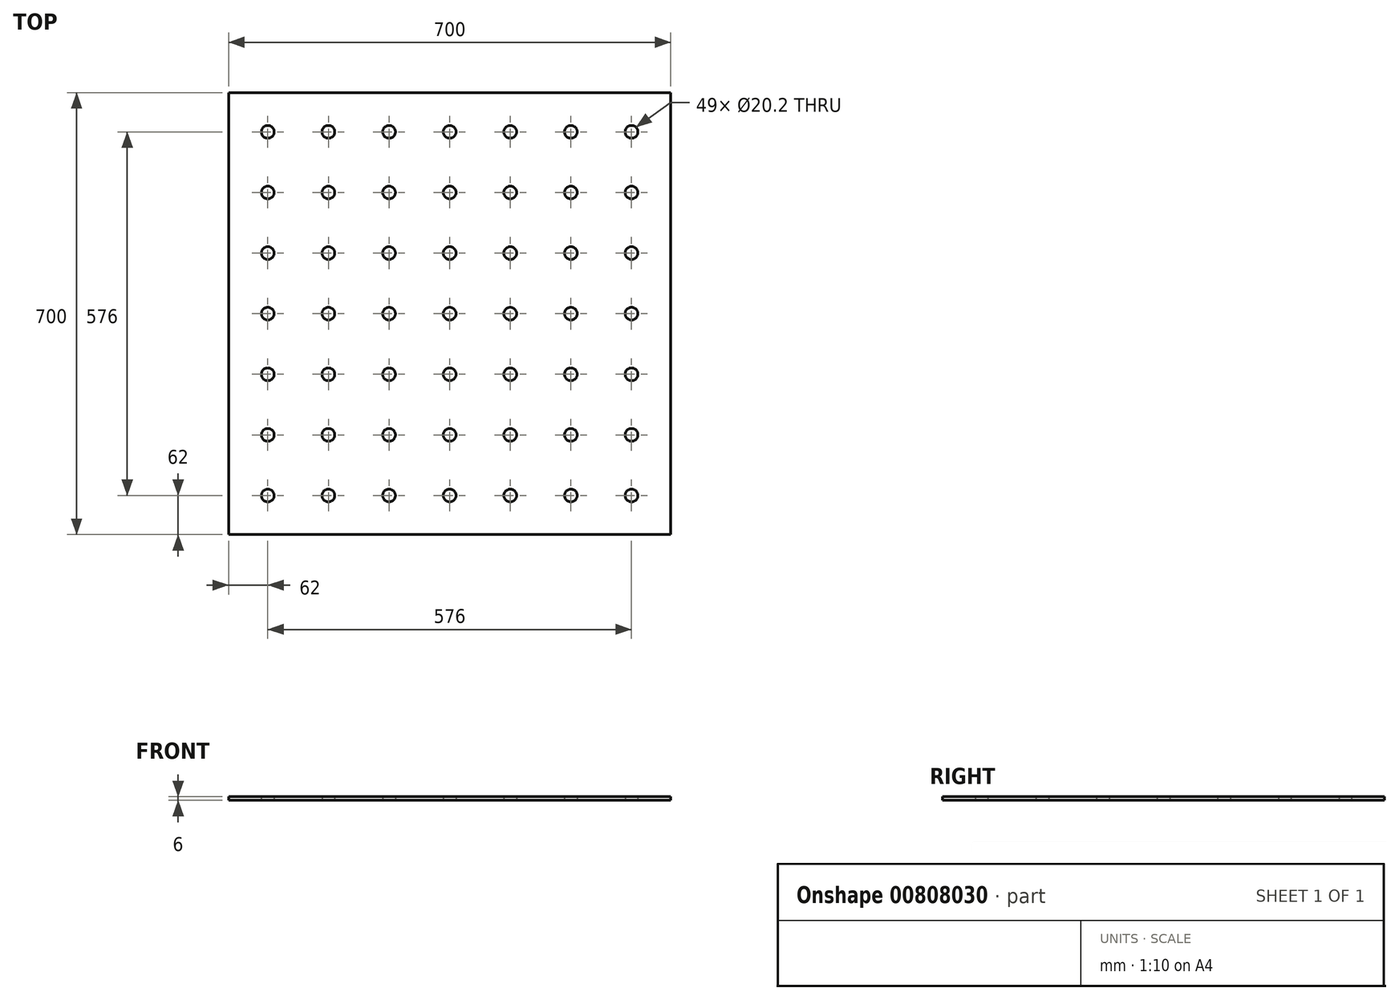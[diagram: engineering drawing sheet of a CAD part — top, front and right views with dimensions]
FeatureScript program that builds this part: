
annotation { "Feature Type Name" : "Feature", "Feature Type Description" : "" }
export const myFeature = defineFeature(function(context is Context, id is Id, definition is map)
    precondition{}
    {
        {
            var Q0;
            Q0=qCreatedBy(makeId("Top.planeOp"),FACE);
            var sketch = newSketch(context, id + "F0", { "sketchPlane" : qUnion([Q0])});
            skLineSegment(sketch, "E0.bottom", {"start": v(-350, 350) * mm, "end": v(350, 350) * mm});
            skLineSegment(sketch, "E0.top", {"start": v(-350, -350) * mm, "end": v(350, -350) * mm});
            skLineSegment(sketch, "E0.left", {"start": v(-350, 350) * mm, "end": v(-350, -350) * mm});
            skLineSegment(sketch, "E0.right", {"start": v(350, 350) * mm, "end": v(350, -350) * mm});
            skPoint(sketch, "E0.middle", {"position": v(0, 0) * mm});
            skLineSegment(sketch, "E1", {"start": v(0, 350) * mm, "end": v(0, -350) * mm, "construction": true});
            skCircle(sketch, "E2", {"center": v(0, 0) * mm, "radius": 10.1 * mm});
            skCircle(sketch, "E3.1.0.0", {"center": v(96, 0) * mm, "radius": 10.1 * mm});
            skCircle(sketch, "E3.2.0.0", {"center": v(192, 0) * mm, "radius": 10.1 * mm});
            skLineSegment(sketch, "E3.direction1", {"start": v(0, 0) * mm, "end": v(96, 0) * mm, "construction": true});
            skCircle(sketch, "E4.0.3.0", {"center": v(288, 0) * mm, "radius": 10.1 * mm});
            skCircle(sketch, "E5.MirrorC", {"center": v(-96, 0) * mm, "radius": 10.1 * mm});
            skCircle(sketch, "E6.MirrorC", {"center": v(-192, 0) * mm, "radius": 10.1 * mm});
            skCircle(sketch, "E7.MirrorC", {"center": v(-288, 0) * mm, "radius": 10.1 * mm});
            skCircle(sketch, "E8", {"center": v(0, 96) * mm, "radius": 10.1 * mm});
            skCircle(sketch, "E9", {"center": v(0, 192) * mm, "radius": 10.1 * mm});
            skCircle(sketch, "E10", {"center": v(0, 288) * mm, "radius": 10.1 * mm});
            skCircle(sketch, "E11.1.0.0", {"center": v(96, 96) * mm, "radius": 10.1 * mm});
            skCircle(sketch, "E11.2.0.0", {"center": v(192, 96) * mm, "radius": 10.1 * mm});
            skCircle(sketch, "E11.3.0.0", {"center": v(288, 96) * mm, "radius": 10.1 * mm});
            skLineSegment(sketch, "E11.direction1", {"start": v(0, 96) * mm, "end": v(96, 96) * mm, "construction": true});
            skCircle(sketch, "E12.1.0.0", {"center": v(96, 192) * mm, "radius": 10.1 * mm});
            skCircle(sketch, "E12.2.0.0", {"center": v(192, 192) * mm, "radius": 10.1 * mm});
            skCircle(sketch, "E12.3.0.0", {"center": v(288, 192) * mm, "radius": 10.1 * mm});
            skLineSegment(sketch, "E12.direction1", {"start": v(0, 192) * mm, "end": v(96, 192) * mm, "construction": true});
            skCircle(sketch, "E13.1.0.0", {"center": v(96, 288) * mm, "radius": 10.1 * mm});
            skCircle(sketch, "E13.2.0.0", {"center": v(192, 288) * mm, "radius": 10.1 * mm});
            skCircle(sketch, "E13.3.0.0", {"center": v(288, 288) * mm, "radius": 10.1 * mm});
            skLineSegment(sketch, "E13.direction1", {"start": v(0, 288) * mm, "end": v(96, 288) * mm, "construction": true});
            skCircle(sketch, "E14.MirrorC", {"center": v(-96, 288) * mm, "radius": 10.1 * mm});
            skCircle(sketch, "E15.MirrorC", {"center": v(-192, 288) * mm, "radius": 10.1 * mm});
            skCircle(sketch, "E16.MirrorC", {"center": v(-288, 288) * mm, "radius": 10.1 * mm});
            skCircle(sketch, "E17.MirrorC", {"center": v(-288, 192) * mm, "radius": 10.1 * mm});
            skCircle(sketch, "E18.MirrorC", {"center": v(-192, 192) * mm, "radius": 10.1 * mm});
            skCircle(sketch, "E19.MirrorC", {"center": v(-96, 192) * mm, "radius": 10.1 * mm});
            skCircle(sketch, "E20.MirrorC", {"center": v(-96, 96) * mm, "radius": 10.1 * mm});
            skCircle(sketch, "E21.MirrorC", {"center": v(-192, 96) * mm, "radius": 10.1 * mm});
            skCircle(sketch, "E22.MirrorC", {"center": v(-288, 96) * mm, "radius": 10.1 * mm});
            skCircle(sketch, "E23.MirrorC", {"center": v(-96, -96) * mm, "radius": 10.1 * mm});
            skCircle(sketch, "E24.MirrorC", {"center": v(-96, -192) * mm, "radius": 10.1 * mm});
            skCircle(sketch, "E25.MirrorC", {"center": v(-192, -96) * mm, "radius": 10.1 * mm});
            skCircle(sketch, "E26.MirrorC", {"center": v(-192, -192) * mm, "radius": 10.1 * mm});
            skCircle(sketch, "E27.MirrorC", {"center": v(-288, -192) * mm, "radius": 10.1 * mm});
            skCircle(sketch, "E28.MirrorC", {"center": v(-288, -96) * mm, "radius": 10.1 * mm});
            skCircle(sketch, "E29.MirrorC", {"center": v(-96, -288) * mm, "radius": 10.1 * mm});
            skCircle(sketch, "E30.MirrorC", {"center": v(-192, -288) * mm, "radius": 10.1 * mm});
            skCircle(sketch, "E31.MirrorC", {"center": v(-288, -288) * mm, "radius": 10.1 * mm});
            skCircle(sketch, "E32.MirrorC", {"center": v(288, -96) * mm, "radius": 10.1 * mm});
            skCircle(sketch, "E33.MirrorC", {"center": v(192, -96) * mm, "radius": 10.1 * mm});
            skCircle(sketch, "E34.MirrorC", {"center": v(96, -96) * mm, "radius": 10.1 * mm});
            skCircle(sketch, "E35.MirrorC", {"center": v(192, -192) * mm, "radius": 10.1 * mm});
            skCircle(sketch, "E36.MirrorC", {"center": v(288, -192) * mm, "radius": 10.1 * mm});
            skCircle(sketch, "E37.MirrorC", {"center": v(96, -192) * mm, "radius": 10.1 * mm});
            skCircle(sketch, "E38.MirrorC", {"center": v(96, -288) * mm, "radius": 10.1 * mm});
            skCircle(sketch, "E39.MirrorC", {"center": v(192, -288) * mm, "radius": 10.1 * mm});
            skCircle(sketch, "E40.MirrorC", {"center": v(288, -288) * mm, "radius": 10.1 * mm});
            skCircle(sketch, "E41.MirrorC", {"center": v(0, -96) * mm, "radius": 10.1 * mm});
            skCircle(sketch, "E42.MirrorC", {"center": v(0, -192) * mm, "radius": 10.1 * mm});
            skCircle(sketch, "E43.MirrorC", {"center": v(0, -288) * mm, "radius": 10.1 * mm});
            skSolve(sketch);
        }
        {
            var Q0;
            Q0=makeQuery(id+"F0.imprint","IMPRINT",FACE,{"disambiguationData":[TD([[makeQuery(id+"F0.imprint","IMPRINT",EDGE,{"derivedFrom":sQuery(id+"F0.wireOp",EDGE,"E0.bottom")}),-1.0]])]});
            extrude(context, id + "F1", {"entities" : qUnion([Q0]), "depth" : 6 * mm, "offsetDistance" : 25 * mm});
        }
    });
